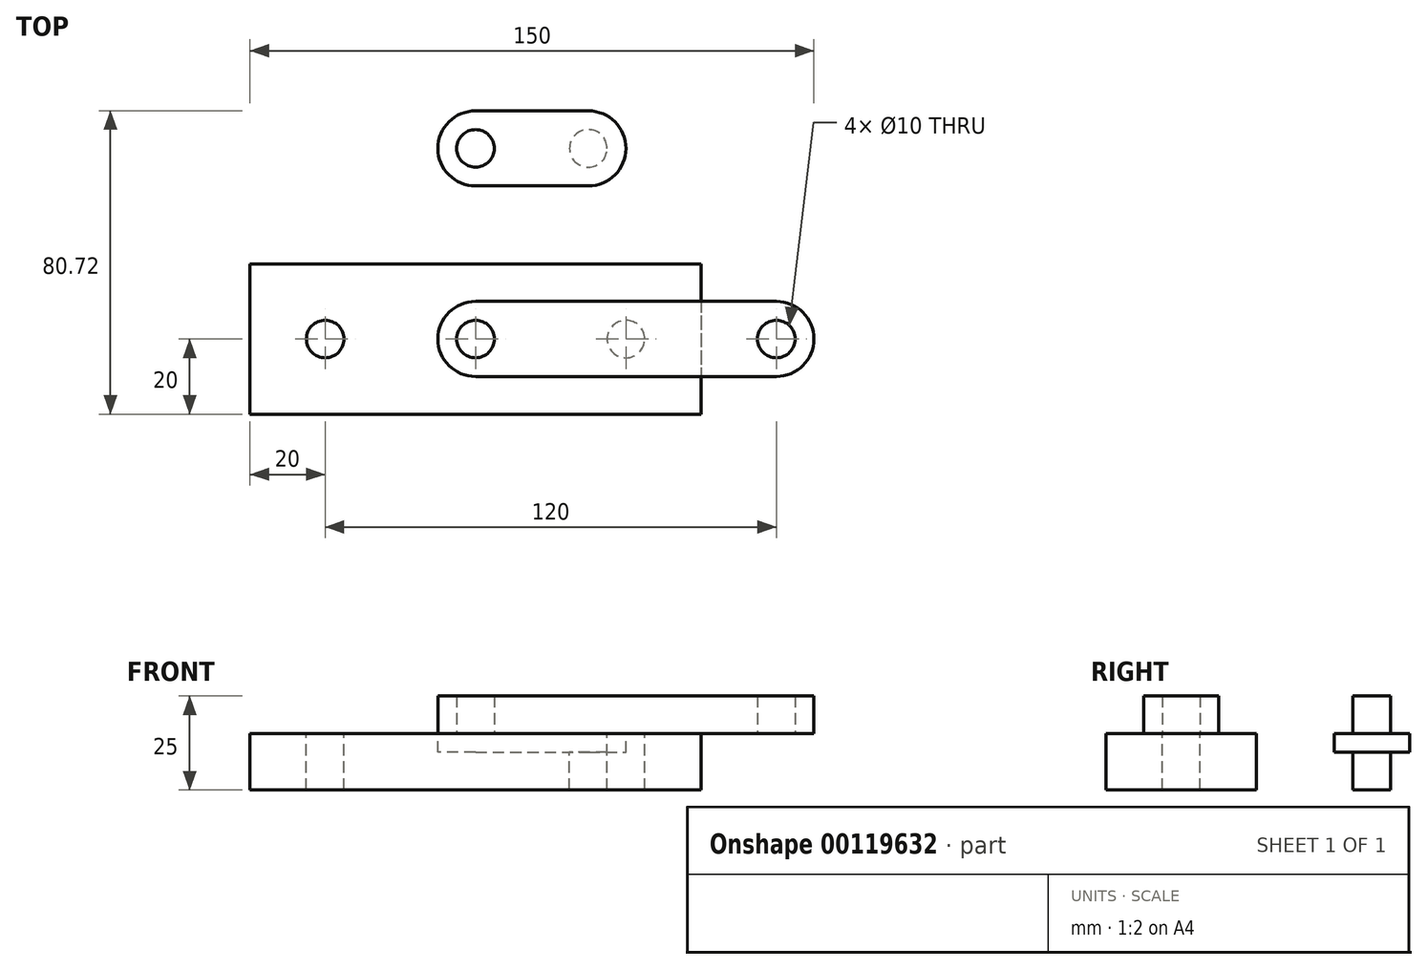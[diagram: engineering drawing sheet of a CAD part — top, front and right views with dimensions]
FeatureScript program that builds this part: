
annotation { "Feature Type Name" : "Feature", "Feature Type Description" : "" }
export const myFeature = defineFeature(function(context is Context, id is Id, definition is map)
    precondition{}
    {
        {
            var Q0;
            Q0=qCreatedBy(makeId("Top.planeOp"),FACE);
            var sketch = newSketch(context, id + "F0", { "sketchPlane" : qUnion([Q0])});
            skLineSegment(sketch, "E0.bottom", {"start": v(-60, 20) * mm, "end": v(60, 20) * mm});
            skLineSegment(sketch, "E0.top", {"start": v(-60, -20) * mm, "end": v(60, -20) * mm});
            skLineSegment(sketch, "E0.left", {"start": v(-60, 20) * mm, "end": v(-60, -20) * mm});
            skLineSegment(sketch, "E0.right", {"start": v(60, 20) * mm, "end": v(60, -20) * mm});
            skCircle(sketch, "E1", {"center": v(-40, 0) * mm, "radius": 5 * mm});
            skCircle(sketch, "E2", {"center": v(40, 0) * mm, "radius": 5 * mm});
            skSolve(sketch);
        }
        {
            var Q0;
            Q0 = qSketchRegion(id + "F0", true);
            extrude(context, id + "F1", {"entities" : qUnion([Q0]), "oppositeDirection" : true, "depth" : 15 * mm});
        }
        {
            var Q0;
            Q0=qCreatedBy(makeId("Top.planeOp"),FACE);
            var sketch = newSketch(context, id + "F2", { "sketchPlane" : qUnion([Q0])});
            skLineSegment(sketch, "E3", {"start": v(0, 60.72) * mm, "end": v(30, 60.72) * mm});
            skLineSegment(sketch, "E4", {"start": v(0, 40.72) * mm, "end": v(30, 40.72) * mm});
            skArc(sketch, "E5", {"start": v(30, 40.72) * mm, "mid": v(40, 50.72) * mm, "end": v(30, 60.72) * mm});
            skArc(sketch, "E6", {"start": v(0, 60.72) * mm, "mid": v(-10, 50.72) * mm, "end": v(0, 40.72) * mm});
            skCircle(sketch, "E7", {"center": v(0, 50.72) * mm, "radius": 5 * mm});
            skCircle(sketch, "E8", {"center": v(30, 50.72) * mm, "radius": 5 * mm});
            skSolve(sketch);
        }
        {
            var Q0;
            Q0 = qSketchRegion(id + "F2", true);
            extrude(context, id + "F3", {"entities" : qUnion([Q0]), "oppositeDirection" : true, "depth" : 5 * mm});
        }
        {
            var Q0;
            Q0=makeQuery(id+"F2.imprint","IMPRINT",FACE,{"disambiguationData":[TD([[makeQuery(id+"F2.imprint","IMPRINT",EDGE,{"derivedFrom":sQuery(id+"F2.wireOp",EDGE,"E7")}),1.0]])]});
            var Q1;
            Q1=sQuery(id+"F2.wireOp",EDGE,"E7");
            var Q2;
            Q2=makeQuery(id+"F3.opExtrude","CAP_FACE",FACE,{"disambiguationData":[OSD([sQuery(id+"F2.wireOp",EDGE,"E3"),sQuery(id+"F2.wireOp",EDGE,"E4"),sQuery(id+"F2.wireOp",EDGE,"E5"),sQuery(id+"F2.wireOp",EDGE,"E6"),sQuery(id+"F2.wireOp",EDGE,"E7"),sQuery(id+"F2.wireOp",EDGE,"E8")])],"isStart":false});
            extrude(context, id + "F4", {"entities" : qUnion([Q0]), "operationType" : NewBodyOperationType.ADD, "surfaceEntities" : qUnion([Q1]), "depth" : 10 * mm, "hasSecondDirection" : true, "secondDirectionBound" : SecondDirectionBoundingType.UP_TO_SURFACE, "secondDirectionOppositeDirection" : true, "secondDirectionBoundEntityFace" : qUnion([Q2]), "secondDirectionDepth" : 25 * mm});
        }
        {
            var Q0;
            Q0=makeQuery(id+"F2.imprint","IMPRINT",FACE,{"disambiguationData":[TD([[makeQuery(id+"F2.imprint","IMPRINT",EDGE,{"derivedFrom":sQuery(id+"F2.wireOp",EDGE,"E8")}),1.0]])]});
            var Q1;
            Q1=sQuery(id+"F2.wireOp",EDGE,"E8");
            extrude(context, id + "F5", {"entities" : qUnion([Q0]), "operationType" : NewBodyOperationType.ADD, "surfaceEntities" : qUnion([Q1]), "oppositeDirection" : true, "depth" : 15 * mm});
        }
        {
            var Q0;
            Q0=qCreatedBy(makeId("Top.planeOp"),FACE);
            var sketch = newSketch(context, id + "F6", { "sketchPlane" : qUnion([Q0])});
            skLineSegment(sketch, "E9", {"start": v(0, 10) * mm, "end": v(80, 10) * mm});
            skLineSegment(sketch, "E10", {"start": v(0, -10) * mm, "end": v(80, -10) * mm});
            skArc(sketch, "E11", {"start": v(80, -10) * mm, "mid": v(90, 0) * mm, "end": v(80, 10) * mm});
            skArc(sketch, "E12", {"start": v(0, 10) * mm, "mid": v(-10, 0) * mm, "end": v(0, -10) * mm});
            skCircle(sketch, "E13", {"center": v(0, 0) * mm, "radius": 5 * mm});
            skCircle(sketch, "E14", {"center": v(80, 0) * mm, "radius": 5 * mm});
            skSolve(sketch);
        }
        {
            var Q0;
            Q0=makeQuery(id+"F6.imprint","IMPRINT",FACE,{"disambiguationData":[TD([[makeQuery(id+"F6.imprint","IMPRINT",EDGE,{"derivedFrom":sQuery(id+"F6.wireOp",EDGE,"E9")}),-1.0]])]});
            extrude(context, id + "F7", {"entities" : qUnion([Q0]), "depth" : 10 * mm});
        }
    });
